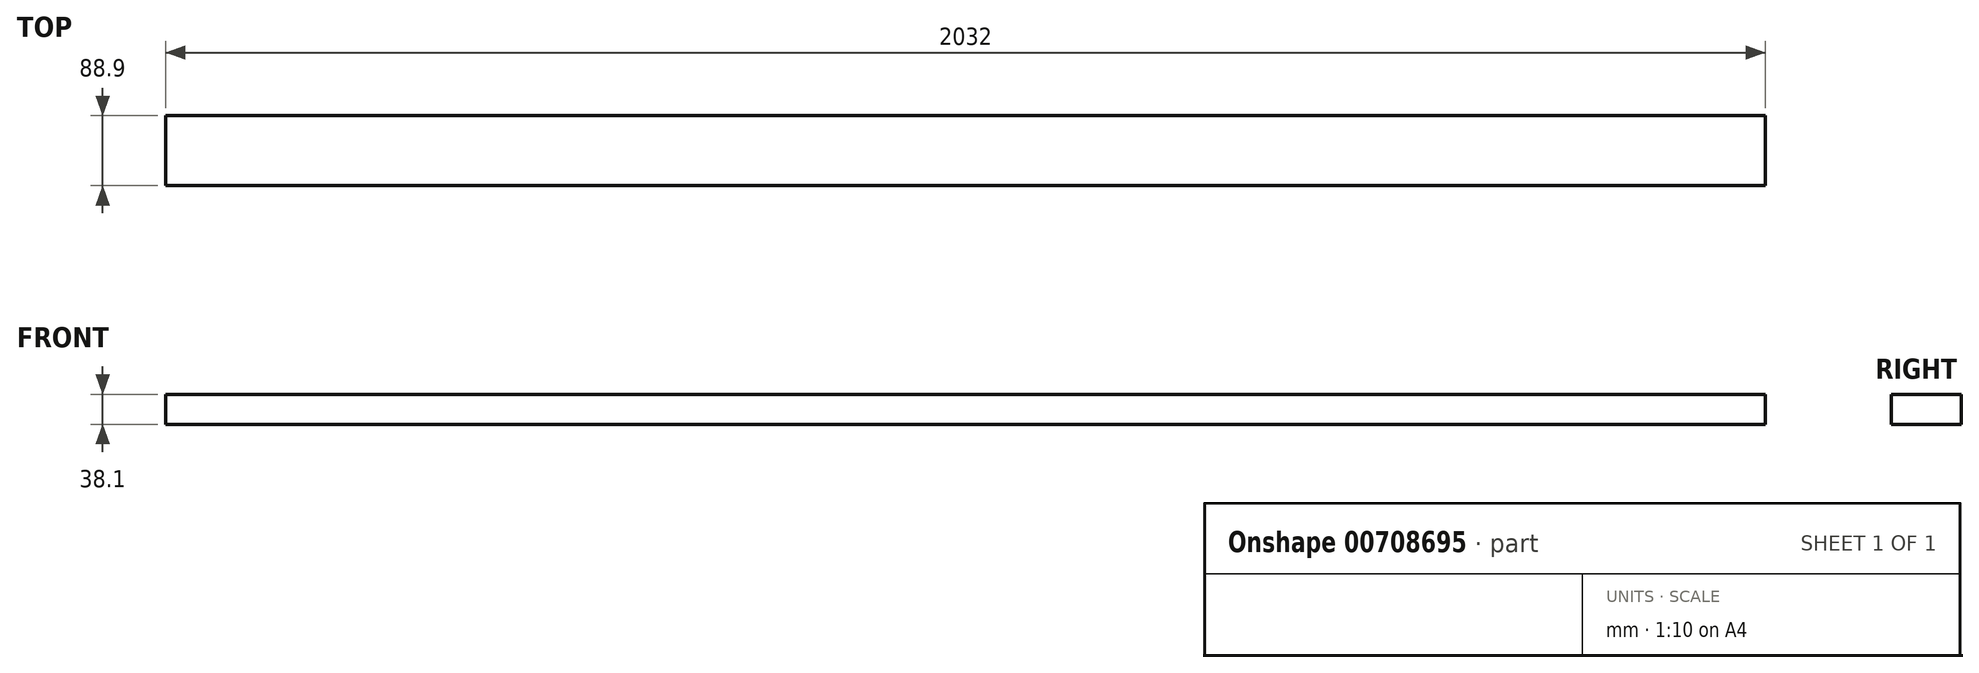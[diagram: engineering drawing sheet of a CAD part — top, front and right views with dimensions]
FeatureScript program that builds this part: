
annotation { "Feature Type Name" : "Feature", "Feature Type Description" : "" }
export const myFeature = defineFeature(function(context is Context, id is Id, definition is map)
    precondition{}
    {
        {
            var Q0;
            Q0=qCreatedBy(makeId("Right.planeOp"),FACE);
            var sketch = newSketch(context, id + "F0", { "sketchPlane" : qUnion([Q0])});
            skLineSegment(sketch, "E0.bottom", {"start": v(44.45, -19.05) * mm, "end": v(-44.45, -19.05) * mm});
            skLineSegment(sketch, "E0.top", {"start": v(44.45, 19.05) * mm, "end": v(-44.45, 19.05) * mm});
            skLineSegment(sketch, "E0.left", {"start": v(44.45, -19.05) * mm, "end": v(44.45, 19.05) * mm});
            skLineSegment(sketch, "E0.right", {"start": v(-44.45, -19.05) * mm, "end": v(-44.45, 19.05) * mm});
            skPoint(sketch, "E0.middle", {"position": v(0, 0) * mm});
            skSolve(sketch);
        }
        {
            var Q0;
            Q0=makeQuery(id+"F0.imprint","IMPRINT",FACE,{"disambiguationData":[TD([[makeQuery(id+"F0.imprint","IMPRINT",EDGE,{"derivedFrom":sQuery(id+"F0.wireOp",EDGE,"E0.bottom")}),-1.0]])]});
            extrude(context, id + "F1", {"entities" : qUnion([Q0]), "endBound" : BoundingType.SYMMETRIC, "depth" : 2032 * mm, "offsetDistance" : 25.4 * mm});
        }
    });
